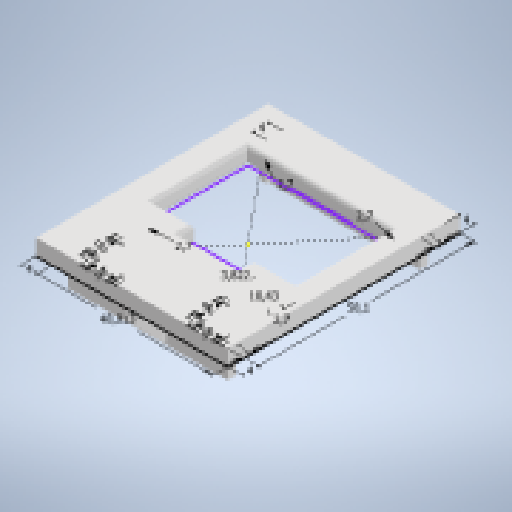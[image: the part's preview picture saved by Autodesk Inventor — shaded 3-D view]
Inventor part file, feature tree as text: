
AUTODESK INVENTOR PART (.ipt)
format: ipt  version: 2024 (Build 280153000, 153)  size: 398,848 bytes
history: native  units: mm
features: extrude x10, sketch x4, chamfer x2, fillet x2
ambient origin geometry x8: Origin, YZ Plane, XZ Plane, XY Plane, X Axis, Y Axis, Z Axis, Center Point
bodies: Volumenkörper1 (feature_tree)
feature tree (18):
  sketch  "Skizze1"  dims[d0=48.013mm d1=58.1mm]
  extrude  "Extrusion1"  Depth=58.1mm
  extrude  "Extrusion2"  Depth=4.0mm
  chamfer  "Fasen1"  Distance=2.0mm
  extrude  "Extrusion3"  Depth=2.0mm
  chamfer  "Fasen2"  Distance=7.0mm
  extrude  "Extrusion4"  Depth=1.0mm
  extrude  "Extrusion5"  Depth=5.0mm
  extrude  "Extrusion6"  Depth=9.0mm
  fillet  "Rundung1"  Radius=3.6mm
  extrude  "Extrusion7"  Depth=1.0mm TaperAngle=0.0deg
  sketch  "Skizze4"  dims[d5=4.0mm d6=2.0mm d7=2.0mm d8=7.0mm d9=0.0mm d10=20.0mm d11=5.0mm d12=9.0mm d13=3.6mm d14=1.8mm d15=0.0mm d16=1.8mm d17=2.0mm d18=45.0deg d19=20.0mm d20=5.0mm d21=9.0mm d22=3.6mm d23=1.8mm d24=0.0mm d25=1.8mm d26=2.0mm d27=45.0deg d28=2.7mm d29=2.7mm d30=2.7mm d31=2.7mm d32=10.43mm d33=3.822mm d34=4.0mm d35=0.0mm d36=3.0mm d37=0.0mm d38=4.0mm d39=0.0mm d40=1.0mm d41=3.0mm d42=0.0mm d43=7.0mm d44=7.0mm d45=9.0mm d46=9.0mm d47=6.0mm d48=6.0mm d49=6.0mm d50=6.0mm d51=7.0mm d52=7.0mm d53=9.0mm d54=9.0mm d55=5.0mm d56=0.0mm d57=2.0mm d58=0.0mm d59=5.0mm d60=0.0mm d61=1.0mm]
  extrude  "Extrusion8"  Depth=2.0mm TaperAngle=45.0deg
  extrude  "Extrusion9"  Depth=1.0mm
  extrude  "Extrusion10"  Depth=5.0mm
  fillet  "Rundung2"  Radius=9.0mm
  sketch  "Skizze2"  dims[d2=4.0mm d3=4.0mm]
  sketch  "Skizze3"  dims[d4=4.0mm]
